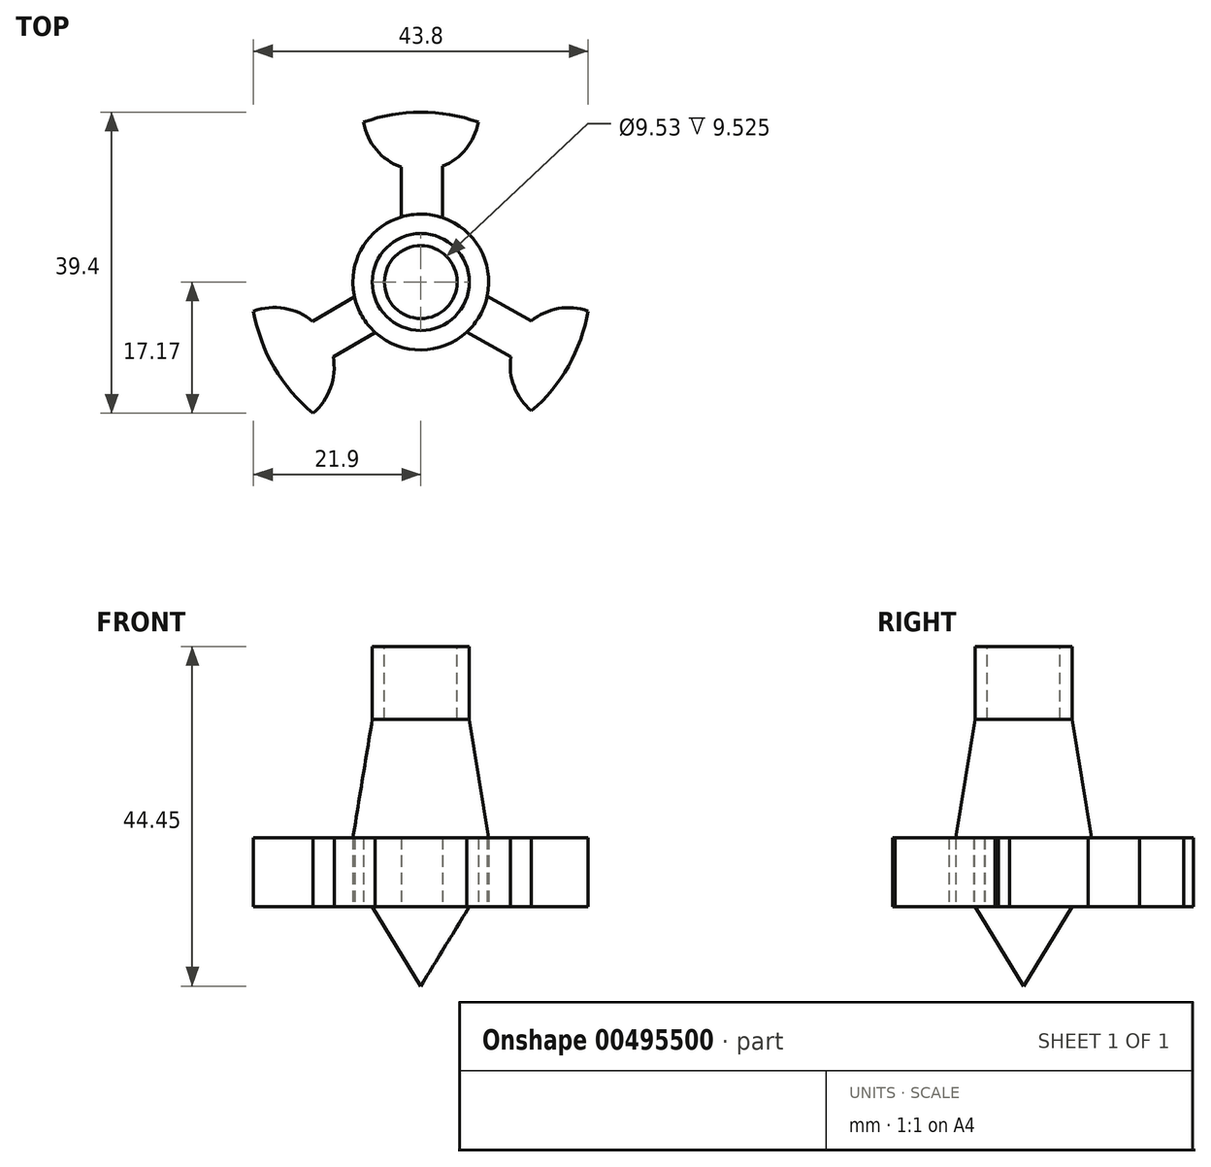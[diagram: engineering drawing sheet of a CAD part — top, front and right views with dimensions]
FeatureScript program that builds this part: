
annotation { "Feature Type Name" : "Feature", "Feature Type Description" : "" }
export const myFeature = defineFeature(function(context is Context, id is Id, definition is map)
    precondition{}
    {
        {
            var Q0;
            Q0=qCreatedBy(makeId("Front.planeOp"),FACE);
            var sketch = newSketch(context, id + "F0", { "sketchPlane" : qUnion([Q0])});
            skLineSegment(sketch, "E0", {"start": v(6.35, 34.05) * mm, "end": v(6.35, 24.53) * mm});
            skLineSegment(sketch, "E1", {"start": v(6.35, 0) * mm, "end": v(0, -10.4) * mm});
            skLineSegment(sketch, "E2.MirrorCS", {"start": v(-6.35, 0) * mm, "end": v(0, -10.4) * mm});
            skLineSegment(sketch, "E3.MirrorCS", {"start": v(-6.35, 34.05) * mm, "end": v(-6.35, 24.53) * mm});
            skLineSegment(sketch, "E4", {"start": v(6.35, 0) * mm, "end": v(22.23, 0) * mm});
            skLineSegment(sketch, "E5", {"start": v(22.23, 0) * mm, "end": v(22.23, 9.01) * mm});
            skLineSegment(sketch, "E6", {"start": v(22.23, 9.01) * mm, "end": v(8.89, 9.01) * mm});
            skLineSegment(sketch, "E7.MirrorCS", {"start": v(-22.23, 9.01) * mm, "end": v(-8.9, 9.01) * mm});
            skLineSegment(sketch, "E8.MirrorCS", {"start": v(-22.23, 0) * mm, "end": v(-22.23, 9.01) * mm});
            skLineSegment(sketch, "E9.MirrorCS", {"start": v(-6.35, 0) * mm, "end": v(-22.23, 0) * mm});
            skLineSegment(sketch, "E10", {"start": v(6.35, 24.53) * mm, "end": v(8.89, 9.01) * mm});
            skLineSegment(sketch, "E11", {"start": v(-6.35, 24.53) * mm, "end": v(-8.9, 9.01) * mm});
            skLineSegment(sketch, "E12", {"start": v(-6.35, 34.05) * mm, "end": v(6.35, 34.05) * mm});
            skLineSegment(sketch, "E13", {"start": v(0, -10.4) * mm, "end": v(0, 34.05) * mm});
            skSolve(sketch);
        }
        {
            var Q0;
            {var subQ0=sQuery(id+"F0.wireOp",EDGE,"E0");Q0=makeQuery(id+"F0.imprint","IMPRINT",FACE,{"disambiguationData":[TD([[makeQuery(id+"F0.imprint","IMPRINT",EDGE,{"derivedFrom":subQ0}),-1.0]])]});}
            var Q1;
            Q1=sQuery(id+"F0.wireOp",EDGE,"E13");
            revolve(context, id + "F1", {"entities" : qUnion([Q0]), "axis" : qUnion([Q1]), "revolveType" : RevolveType.FULL});
        }
        {
            var Q0;
            Q0=qCreatedBy(makeId("Top.planeOp"),FACE);
            var sketch = newSketch(context, id + "F2", { "sketchPlane" : qUnion([Q0])});
            skCircle(sketch, "E14", {"center": v(0, 0) * mm, "radius": 22.23 * mm});
            skArc(sketch, "E15", {"start": v(-7.5, 20.92) * mm, "mid": v(-5.82, 17.31) * mm, "end": v(-2.55, 15.05) * mm});
            skCircle(sketch, "E16", {"center": v(0, 0) * mm, "radius": 8.9 * mm});
            skPoint(sketch, "E17.orphan", {"position": v(0.8, -0.05) * mm});
            skArc(sketch, "E18.trimOffspring", {"start": v(2.83, 15.15) * mm, "mid": v(5.92, 17.42) * mm, "end": v(7.5, 20.92) * mm});
            skArc(sketch, "E19", {"start": v(-14.11, -17.17) * mm, "mid": v(-11.8, -13.83) * mm, "end": v(-11.47, -9.8) * mm});
            skArc(sketch, "E20", {"start": v(21.9, -3.8) * mm, "mid": v(18, -3.47) * mm, "end": v(14.46, -5.11) * mm});
            skLineSegment(sketch, "E21", {"start": v(-2.55, 15.05) * mm, "end": v(-2.55, 8.52) * mm});
            skLineSegment(sketch, "E22", {"start": v(2.83, 15.15) * mm, "end": v(2.83, 8.43) * mm});
            skLineSegment(sketch, "E23.trimOffspring", {"start": v(-11.47, -9.8) * mm, "end": v(-5.97, -6.59) * mm});
            skLineSegment(sketch, "E24.trimOffspring", {"start": v(-14.18, -5.14) * mm, "end": v(-8.68, -1.94) * mm});
            skLineSegment(sketch, "E25", {"start": v(11.8, -9.8) * mm, "end": v(6.04, -6.52) * mm});
            skLineSegment(sketch, "E26.MirrorCS", {"start": v(14.46, -5.11) * mm, "end": v(8.7, -1.84) * mm});
            skArc(sketch, "E27.trimOffspring", {"start": v(11.8, -9.8) * mm, "mid": v(12.2, -13.68) * mm, "end": v(14.49, -16.85) * mm});
            skArc(sketch, "E28.trimOffspring", {"start": v(-14.18, -5.14) * mm, "mid": v(-17.86, -3.44) * mm, "end": v(-21.9, -3.8) * mm});
            skSolve(sketch);
        }
        {
            var Q0;
            {var subQ0=sQuery(id+"F2.wireOp",EDGE,"E19");Q0=makeQuery(id+"F2.imprint","IMPRINT",FACE,{"disambiguationData":[TD([[makeQuery(id+"F2.imprint","IMPRINT",EDGE,{"derivedFrom":subQ0}),-1.0]])]});}
            var Q1;
            {var subQ0=sQuery(id+"F2.wireOp",EDGE,"E18.trimOffspring");Q1=makeQuery(id+"F2.imprint","IMPRINT",FACE,{"disambiguationData":[TD([[makeQuery(id+"F2.imprint","IMPRINT",EDGE,{"derivedFrom":subQ0}),-1.0]])]});}
            var Q2;
            {var subQ3=sQuery(id+"F2.wireOp",EDGE,"E15");Q2=makeQuery(id+"F2.imprint","IMPRINT",FACE,{"disambiguationData":[TD([[makeQuery(id+"F2.imprint","IMPRINT",EDGE,{"derivedFrom":subQ3}),-1.0]])]});}
            extrude(context, id + "F3", {"entities" : qUnion([Q0, Q1, Q2]), "operationType" : NewBodyOperationType.REMOVE, "depth" : 14.1 * mm});
        }
        {
            var Q0;
            Q0=makeQuery(id+"F1.opRevolve","SWEPT_FACE",FACE,{"disambiguationData":[OSD([sQuery(id+"F0.wireOp",EDGE,"E12")])]});
            var sketch = newSketch(context, id + "F4", { "sketchPlane" : qUnion([Q0])});
            skCircle(sketch, "E29", {"center": v(0, 0) * mm, "radius": 4.76 * mm});
            skSolve(sketch);
        }
        {
            var Q0;
            Q0=makeQuery(id+"F4.imprint","IMPRINT",FACE,{"disambiguationData":[TD([[makeQuery(id+"F4.imprint","IMPRINT",EDGE,{"derivedFrom":sQuery(id+"F4.wireOp",EDGE,"E29")}),1.0]])]});
            extrude(context, id + "F5", {"entities" : qUnion([Q0]), "operationType" : NewBodyOperationType.REMOVE, "oppositeDirection" : true, "depth" : 9.52 * mm});
        }
    });
